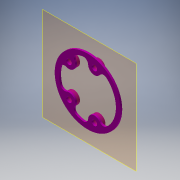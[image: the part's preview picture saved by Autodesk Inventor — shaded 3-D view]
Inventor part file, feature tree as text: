
AUTODESK INVENTOR PART (.ipt)
format: ipt  version: 2017 (Build 210142000, 142)  size: 201,728 bytes
history: native  units: in
note: dims shown in document units (in); Inventor stores cm internally (conversion verified against a paired STEP export)
features: other x4, reference x3, extrude x2, sketch x2, plane x1, fillet x1
ambient origin geometry x8: Origin, YZ Plane, XZ Plane, XY Plane, X Axis, Y Axis, Z Axis, Center Point
bodies: Solid1 (feature_tree)
feature tree (13):
  plane  "Work Plane1"
  extrude  "Extrusion1"  Depth=0.1in
  fillet  "Fillet1"  Radius=0.1in
  extrude  "Extrusion2"  Depth=0.085in
  sketch  "Sketch1"  dims[d0=0.1in d1=0.1in d2=0.1in]
  reference  "Reference1"
  reference  "Reference2"
  sketch  "Sketch2"  dims[d3=0.1in d4=0.15in d5=0.1in d6=0.15in d7=0.05in d8=0.125in d9=0.1in d10=0.125in d11=0.125in d12=0.125in d13=0.125in d14=0.05in d15=0.0in d16=0.125in d17=0.005in d18=0.085in d19=0.0in]
  reference  "Reference3"
  other  "<userpath>\Documents\Inventor\PixyCam and Gimbal\Assembly2.iam"
  other  "Assembly2.iam"
  other  "LEDRing:1"
  other  "frontCase:1"
